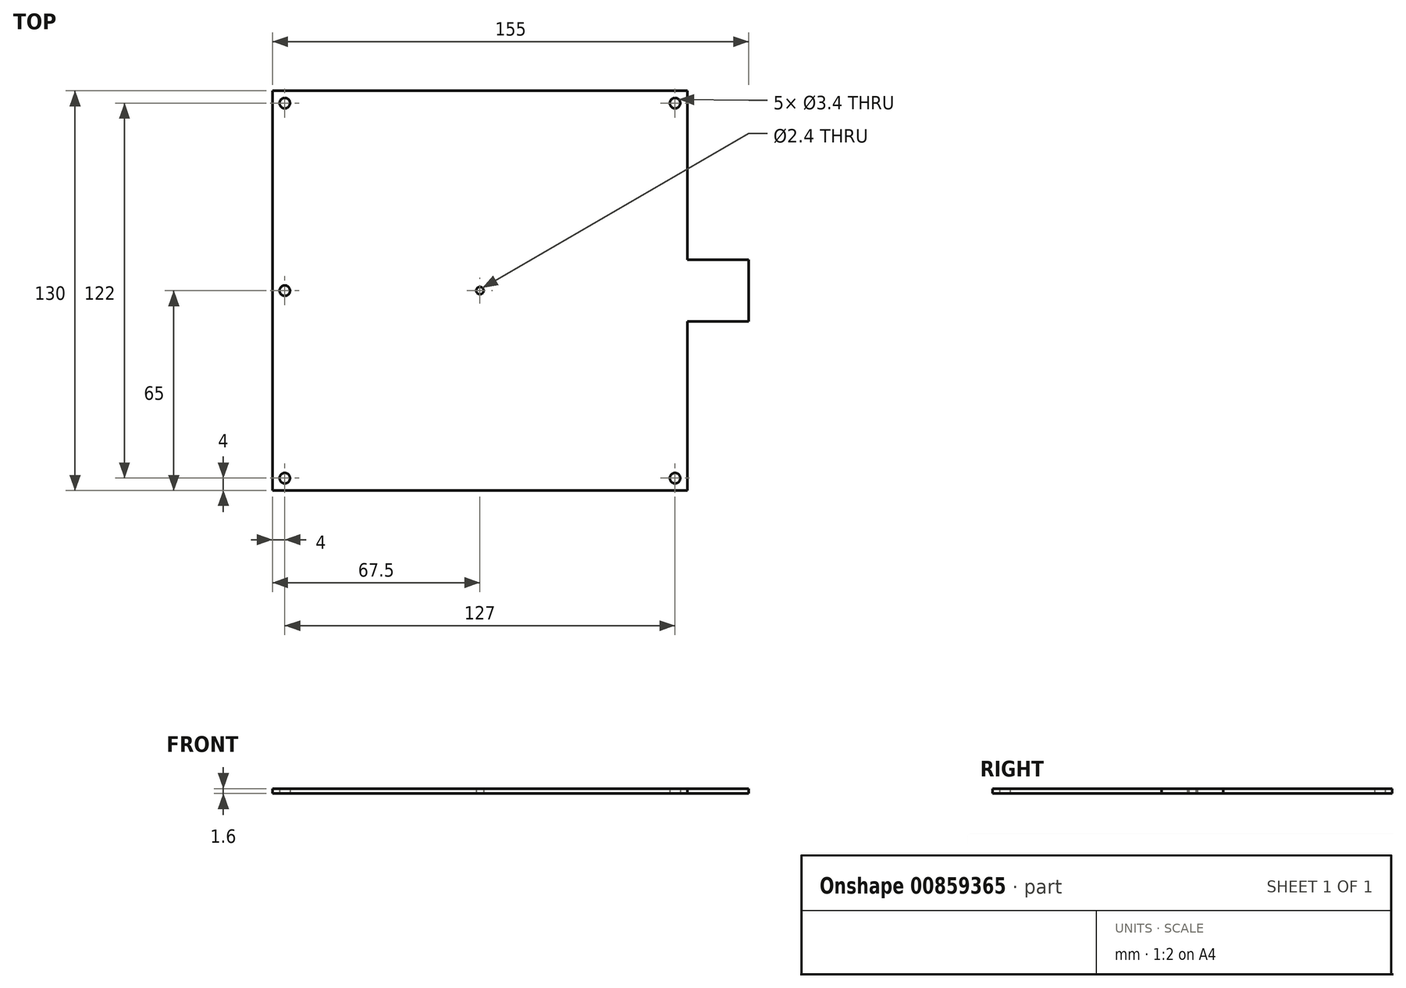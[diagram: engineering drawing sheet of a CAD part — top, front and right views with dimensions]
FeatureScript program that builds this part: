
annotation { "Feature Type Name" : "Feature", "Feature Type Description" : "" }
export const myFeature = defineFeature(function(context is Context, id is Id, definition is map)
    precondition{}
    {
        {
            var Q0;
            Q0=qCreatedBy(makeId("Top.planeOp"), FACE);
            var sketch = newSketch(context, id + "F0", { "sketchPlane" : qUnion([Q0])});
            skLineSegment(sketch, "E0.bottom", {"start": v(-67.5, 65) * mm, "end": v(67.5, 65) * mm});
            skLineSegment(sketch, "E0.top", {"start": v(-67.5, -65) * mm, "end": v(67.5, -65) * mm});
            skLineSegment(sketch, "E0.left", {"start": v(-67.5, 65) * mm, "end": v(-67.5, -65) * mm});
            skLineSegment(sketch, "E0.right", {"start": v(67.5, 65) * mm, "end": v(67.5, -65) * mm});
            skLineSegment(sketch, "E1.bottom", {"start": v(63.5, -61) * mm, "end": v(-63.5, -61) * mm, "construction": true});
            skLineSegment(sketch, "E1.top", {"start": v(63.5, 61) * mm, "end": v(-63.5, 61) * mm, "construction": true});
            skLineSegment(sketch, "E1.left", {"start": v(63.5, -61) * mm, "end": v(63.5, 61) * mm, "construction": true});
            skLineSegment(sketch, "E1.right", {"start": v(-63.5, -61) * mm, "end": v(-63.5, 61) * mm, "construction": true});
            skPoint(sketch, "E1.middle", {"position": v(0, 0) * mm});
            skLineSegment(sketch, "E2", {"start": v(0, 0) * mm, "end": v(0, 65) * mm, "construction": true});
            skLineSegment(sketch, "E3", {"start": v(0, 0) * mm, "end": v(67.5, 0) * mm, "construction": true});
            skCircle(sketch, "E4", {"center": v(63.5, 61) * mm, "radius": 1.7 * mm});
            skCircle(sketch, "E5", {"center": v(-63.5, 0) * mm, "radius": 1.7 * mm});
            skCircle(sketch, "E6", {"center": v(63.5, -61) * mm, "radius": 1.7 * mm});
            skCircle(sketch, "E7", {"center": v(-63.5, 61) * mm, "radius": 1.7 * mm});
            skCircle(sketch, "E8", {"center": v(-63.5, -61) * mm, "radius": 1.7 * mm});
            skCircle(sketch, "E9", {"center": v(0, 0) * mm, "radius": 1.2 * mm});
            skLineSegment(sketch, "E10.bottom", {"start": v(67.5, -10) * mm, "end": v(87.5, -10) * mm});
            skLineSegment(sketch, "E10.top", {"start": v(67.5, 10) * mm, "end": v(87.5, 10) * mm});
            skLineSegment(sketch, "E10.left", {"start": v(67.5, -10) * mm, "end": v(67.5, 10) * mm});
            skLineSegment(sketch, "E10.right", {"start": v(87.5, -10) * mm, "end": v(87.5, 10) * mm});
            skSolve(sketch);
        }
        {
            var Q0;
            Q0 = qSketchRegion(id + "F0", true);
            extrude(context, id + "F1", {"entities" : qUnion([Q0]), "depth" : 1.6 * mm, "offsetDistance" : 25 * mm});
        }
    });
